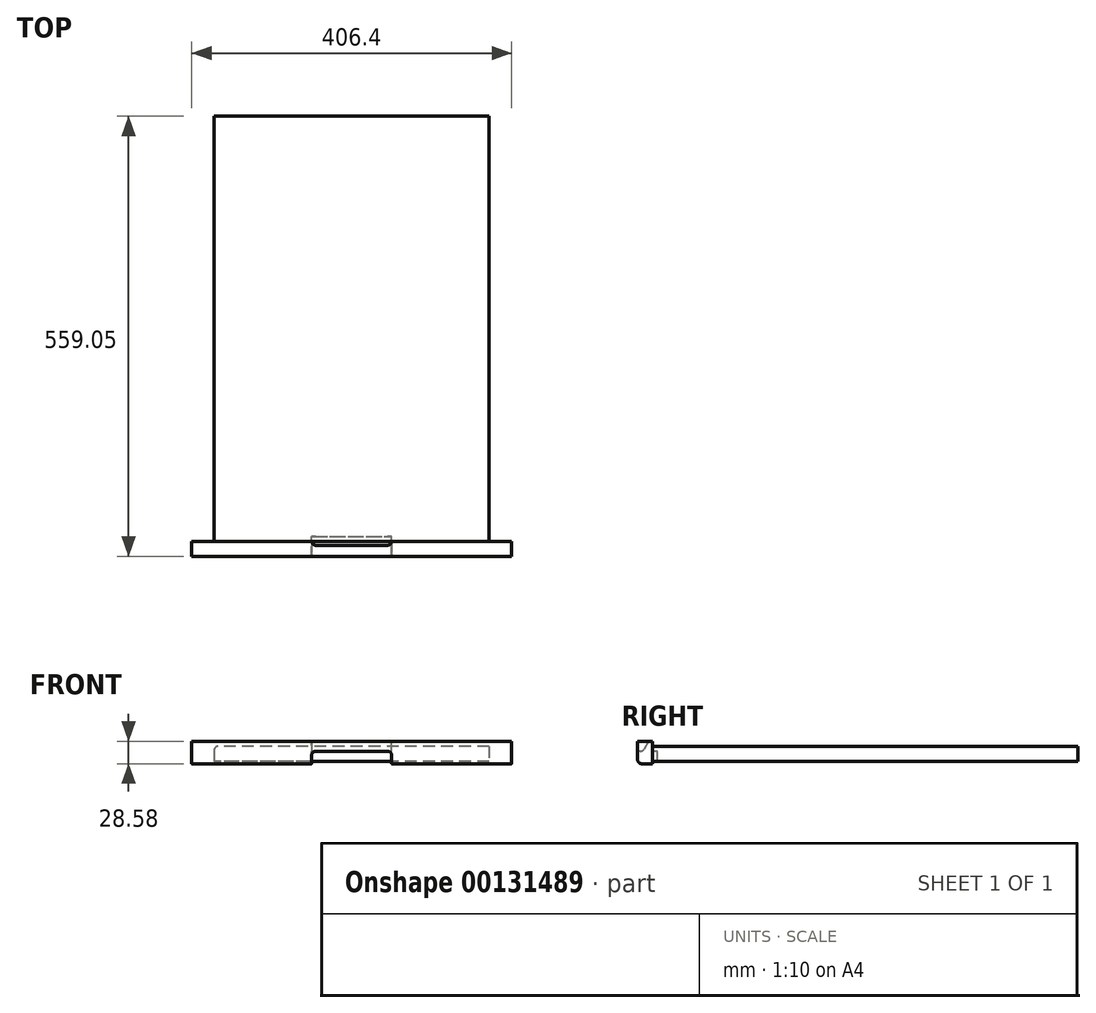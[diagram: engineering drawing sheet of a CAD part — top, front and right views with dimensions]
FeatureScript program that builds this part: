
annotation { "Feature Type Name" : "Feature", "Feature Type Description" : "" }
export const myFeature = defineFeature(function(context is Context, id is Id, definition is map)
    precondition{}
    {
        {
            var Q0;
            Q0=qCreatedBy(makeId("Top.planeOp"),FACE);
            var sketch = newSketch(context, id + "F0", { "sketchPlane" : qUnion([Q0])});
            skLineSegment(sketch, "E0.bottom", {"start": v(174.63, 270) * mm, "end": v(-174.62, 270) * mm});
            skLineSegment(sketch, "E0.top", {"start": v(174.63, -270) * mm, "end": v(-174.63, -270) * mm});
            skLineSegment(sketch, "E0.left", {"start": v(174.63, 270) * mm, "end": v(174.63, -270) * mm});
            skLineSegment(sketch, "E0.right", {"start": v(-174.62, 270) * mm, "end": v(-174.63, -270) * mm});
            skPoint(sketch, "E0.middle", {"position": v(0, 0) * mm});
            skSolve(sketch);
        }
        {
            var Q0;
            Q0 = qSketchRegion(id + "F0", true);
            extrude(context, id + "F1", {"entities" : qUnion([Q0]), "depth" : 19.05 * mm});
        }
        {
            var Q0;
            Q0=makeQuery(id+"F1.opExtrude","SWEPT_FACE",FACE,{"disambiguationData":[OSD([sQuery(id+"F0.wireOp",EDGE,"E0.top")])]});
            var sketch = newSketch(context, id + "F2", { "sketchPlane" : qUnion([Q0])});
            skLineSegment(sketch, "E1.bottom", {"start": v(-203.2, 25.4) * mm, "end": v(203.2, 25.4) * mm});
            skLineSegment(sketch, "E1.top", {"start": v(-203.2, -3.18) * mm, "end": v(203.2, -3.18) * mm});
            skLineSegment(sketch, "E1.left", {"start": v(-203.2, 25.4) * mm, "end": v(-203.2, -3.17) * mm});
            skLineSegment(sketch, "E1.right", {"start": v(203.2, 25.4) * mm, "end": v(203.2, -3.17) * mm});
            skLineSegment(sketch, "E2", {"start": v(-203.2, 11.11) * mm, "end": v(-174.63, 11.11) * mm, "construction": true});
            skLineSegment(sketch, "E3.0", {"start": v(-174.63, 19.05) * mm, "end": v(-174.63, 0) * mm, "construction": true});
            skLineSegment(sketch, "E4.0", {"start": v(174.63, 19.05) * mm, "end": v(-174.63, 19.05) * mm, "construction": true});
            skLineSegment(sketch, "E5.0", {"start": v(174.63, 19.05) * mm, "end": v(174.63, 0) * mm, "construction": true});
            skLineSegment(sketch, "E6.0", {"start": v(174.63, 0) * mm, "end": v(-174.63, 0) * mm, "construction": true});
            skLineSegment(sketch, "E7.trimOffspring", {"start": v(174.63, 11.11) * mm, "end": v(203.2, 11.11) * mm, "construction": true});
            skSolve(sketch);
        }
        {
            var Q0;
            Q0 = qSketchRegion(id + "F2", true);
            extrude(context, id + "F3", {"entities" : qUnion([Q0]), "depth" : 19.05 * mm});
        }
        {
            var Q0;
            Q0=makeQuery(id+"F3.opExtrude","CAP_FACE",FACE,{"disambiguationData":[OSD([sQuery(id+"F2.wireOp",EDGE,"E1.bottom"),sQuery(id+"F2.wireOp",EDGE,"E1.top"),sQuery(id+"F2.wireOp",EDGE,"E1.left"),sQuery(id+"F2.wireOp",EDGE,"E1.right")])],"isStart":false});
            var sketch = newSketch(context, id + "F4", { "sketchPlane" : qUnion([Q0])});
            skLineSegment(sketch, "E8.bottom", {"start": v(-50.8, -3.18) * mm, "end": v(50.8, -3.18) * mm});
            skLineSegment(sketch, "E8.top", {"start": v(-50.8, 12.7) * mm, "end": v(50.8, 12.7) * mm});
            skLineSegment(sketch, "E8.left", {"start": v(-50.8, -3.18) * mm, "end": v(-50.8, 12.7) * mm});
            skLineSegment(sketch, "E8.right", {"start": v(50.8, -3.18) * mm, "end": v(50.8, 12.7) * mm});
            skLineSegment(sketch, "E9", {"start": v(50.8, 12.7) * mm, "end": v(203.2, 12.7) * mm, "construction": true});
            skLineSegment(sketch, "E10", {"start": v(-50.8, 12.7) * mm, "end": v(-203.2, 12.7) * mm, "construction": true});
            skSolve(sketch);
        }
        {
            var Q0;
            Q0 = qSketchRegion(id + "F4", true);
            extrude(context, id + "F5", {"entities" : qUnion([Q0]), "operationType" : NewBodyOperationType.REMOVE, "oppositeDirection" : true, "depth" : 25.4 * mm});
        }
        {
            var Q0;
            Q0=makeQuery(id+"F5.boolean.opBoolean","INTERSECT",EDGE,{"derivedFrom":[makeQuery(id+"F3.opExtrude","CAP_FACE",FACE,{"disambiguationData":[OSD([sQuery(id+"F2.wireOp",EDGE,"E1.bottom"),sQuery(id+"F2.wireOp",EDGE,"E1.top"),sQuery(id+"F2.wireOp",EDGE,"E1.left"),sQuery(id+"F2.wireOp",EDGE,"E1.right")])],"isStart":true}),makeQuery(id+"F5.opExtrude","SWEPT_FACE",FACE,{"disambiguationData":[OSD([sQuery(id+"F4.wireOp",EDGE,"E8.top")])]})]});
            chamfer(context, id + "F6", {"entities" : qUnion([Q0]), "chamferType" : ChamferType.OFFSET_ANGLE, "width" : 21.59 * mm, "oppositeDirection" : false, "angle" : 30 * degree, "tangentPropagation" : true});
        }
        {
            var Q0;
            Q0=makeQuery(id+"F5.boolean.opBoolean","COPY",EDGE,{"derivedFrom":makeQuery(id+"F5.opExtrude","SWEPT_EDGE",EDGE,{"disambiguationData":[OSD([sQuery(id+"F2.wireOp",EDGE,"E1.top"),sQuery(id+"F4.wireOp",EDGE,"E8.bottom"),sQuery(id+"F4.wireOp",EDGE,"E8.left")])]})});
            var Q1;
            Q1=makeQuery(id+"F5.boolean.opBoolean","COPY",EDGE,{"derivedFrom":makeQuery(id+"F5.opExtrude","SWEPT_EDGE",EDGE,{"disambiguationData":[OSD([sQuery(id+"F2.wireOp",EDGE,"E1.top"),sQuery(id+"F4.wireOp",EDGE,"E8.bottom"),sQuery(id+"F4.wireOp",EDGE,"E8.right")])]})});
            var Q2;
            Q2=makeQuery(id+"F6.opChamfer","BLEND_EDGE",EDGE,{"blendedFrom":[makeQuery(id+"F5.boolean.opBoolean","INTERSECT",EDGE,{"derivedFrom":[makeQuery(id+"F3.opExtrude","CAP_FACE",FACE,{"disambiguationData":[OSD([sQuery(id+"F2.wireOp",EDGE,"E1.bottom"),sQuery(id+"F2.wireOp",EDGE,"E1.top"),sQuery(id+"F2.wireOp",EDGE,"E1.left"),sQuery(id+"F2.wireOp",EDGE,"E1.right")])],"isStart":true}),makeQuery(id+"F5.opExtrude","SWEPT_FACE",FACE,{"disambiguationData":[OSD([sQuery(id+"F4.wireOp",EDGE,"E8.top")])]})]}),makeQuery(id+"F5.boolean.opBoolean","COPY",FACE,{"derivedFrom":makeQuery(id+"F5.opExtrude","SWEPT_FACE",FACE,{"disambiguationData":[OSD([sQuery(id+"F4.wireOp",EDGE,"E8.right")])]})})],"blendedInto":[makeQuery(id+"F5.boolean.opBoolean","COPY",FACE,{"derivedFrom":makeQuery(id+"F5.opExtrude","SWEPT_FACE",FACE,{"disambiguationData":[OSD([sQuery(id+"F4.wireOp",EDGE,"E8.right")])]})})]});
            var Q3;
            Q3=makeQuery(id+"FXZCt5cPQfUOwaD_1.boolean.opBoolean","COPY",EDGE,{"derivedFrom":makeQuery(id+"FXZCt5cPQfUOwaD_1.opExtrude","SWEPT_EDGE",EDGE,{"disambiguationData":[OSD([sQuery(id+"FGhspWLTeAS0HlX_1.wireOp",EDGE,"FRW7Mbth-WyWN-BmpX-e6wB-hWx09g5650vy.bottom"),sQuery(id+"FGhspWLTeAS0HlX_1.wireOp",EDGE,"FRW7Mbth-WyWN-BmpX-e6wB-hWx09g5650vy.right")])]})});
            var Q4;
            Q4=makeQuery(id+"F1.opExtrude","CAP_EDGE",EDGE,{"disambiguationData":[OSD([sQuery(id+"F0.wireOp",EDGE,"E0.right")])],"isStart":false});
            var Q5;
            Q5=makeQuery(id+"FXZCt5cPQfUOwaD_1.boolean.opBoolean","COPY",EDGE,{"derivedFrom":makeQuery(id+"FXZCt5cPQfUOwaD_1.opExtrude","CAP_EDGE",EDGE,{"disambiguationData":[OSD([sQuery(id+"FGhspWLTeAS0HlX_1.wireOp",EDGE,"FRW7Mbth-WyWN-BmpX-e6wB-hWx09g5650vy.right")])],"isStart":true})});
            var Q6;
            Q6=makeQuery(id+"F6.opChamfer","BLEND_EDGE",EDGE,{"blendedFrom":[makeQuery(id+"F5.boolean.opBoolean","INTERSECT",EDGE,{"derivedFrom":[makeQuery(id+"F3.opExtrude","CAP_FACE",FACE,{"disambiguationData":[OSD([sQuery(id+"F2.wireOp",EDGE,"E1.bottom"),sQuery(id+"F2.wireOp",EDGE,"E1.top"),sQuery(id+"F2.wireOp",EDGE,"E1.left"),sQuery(id+"F2.wireOp",EDGE,"E1.right")])],"isStart":true}),makeQuery(id+"F5.opExtrude","SWEPT_FACE",FACE,{"disambiguationData":[OSD([sQuery(id+"F4.wireOp",EDGE,"E8.top")])]})]}),makeQuery(id+"F5.boolean.opBoolean","COPY",FACE,{"derivedFrom":makeQuery(id+"F5.opExtrude","SWEPT_FACE",FACE,{"disambiguationData":[OSD([sQuery(id+"F4.wireOp",EDGE,"E8.left")])]})})],"blendedInto":[makeQuery(id+"F5.boolean.opBoolean","COPY",FACE,{"derivedFrom":makeQuery(id+"F5.opExtrude","SWEPT_FACE",FACE,{"disambiguationData":[OSD([sQuery(id+"F4.wireOp",EDGE,"E8.left")])]})})]});
            var Q7;
            Q7=makeQuery(id+"F5.boolean.opBoolean","COPY",EDGE,{"derivedFrom":makeQuery(id+"F5.opExtrude","SWEPT_EDGE",EDGE,{"disambiguationData":[OSD([sQuery(id+"F4.wireOp",EDGE,"E8.top"),sQuery(id+"F4.wireOp",EDGE,"E8.left")])]})});
            var Q8;
            {var subQ0=makeQuery(id+"F5.opExtrude","SWEPT_FACE",FACE,{"disambiguationData":[OSD([sQuery(id+"F4.wireOp",EDGE,"E8.top")])]});Q8=makeQuery(id+"F6.opChamfer","BLEND_EDGE",EDGE,{"blendedFrom":[makeQuery(id+"F5.boolean.opBoolean","INTERSECT",EDGE,{"derivedFrom":[makeQuery(id+"F3.opExtrude","CAP_FACE",FACE,{"disambiguationData":[OSD([sQuery(id+"F2.wireOp",EDGE,"E1.bottom"),sQuery(id+"F2.wireOp",EDGE,"E1.top"),sQuery(id+"F2.wireOp",EDGE,"E1.left"),sQuery(id+"F2.wireOp",EDGE,"E1.right")])],"isStart":true}),subQ0]}),makeQuery(id+"F5.boolean.opBoolean","COPY",FACE,{"derivedFrom":subQ0})],"blendedInto":[makeQuery(id+"F5.boolean.opBoolean","COPY",FACE,{"derivedFrom":subQ0})]});}
            var Q9;
            Q9=makeQuery(id+"F5.boolean.opBoolean","COPY",EDGE,{"derivedFrom":makeQuery(id+"F5.opExtrude","CAP_EDGE",EDGE,{"disambiguationData":[OSD([sQuery(id+"F4.wireOp",EDGE,"E8.top")])],"isStart":true})});
            var Q10;
            Q10=makeQuery(id+"F5.boolean.opBoolean","COPY",EDGE,{"derivedFrom":makeQuery(id+"F5.opExtrude","SWEPT_EDGE",EDGE,{"disambiguationData":[OSD([sQuery(id+"F4.wireOp",EDGE,"E8.top"),sQuery(id+"F4.wireOp",EDGE,"E8.right")])]})});
            var Q11;
            {var subQ0=sQuery(id+"F2.wireOp",EDGE,"E1.right");var subQ1=sQuery(id+"F2.wireOp",EDGE,"E1.left");var subQ2=sQuery(id+"F2.wireOp",EDGE,"E1.top");var subQ3=sQuery(id+"F2.wireOp",EDGE,"E1.bottom");Q11=makeQuery(id+"F6.opChamfer","BLEND_EDGE",EDGE,{"blendedFrom":[makeQuery(id+"F5.boolean.opBoolean","INTERSECT",EDGE,{"derivedFrom":[makeQuery(id+"F3.opExtrude","CAP_FACE",FACE,{"disambiguationData":[OSD([subQ3,subQ2,subQ1,subQ0])],"isStart":true}),makeQuery(id+"F5.opExtrude","SWEPT_FACE",FACE,{"disambiguationData":[OSD([sQuery(id+"F4.wireOp",EDGE,"E8.top")])]})]}),makeQuery(id+"F3.opExtrude","CAP_FACE",FACE,{"disambiguationData":[OSD([subQ3,subQ2,subQ1,subQ0])],"isStart":false})],"blendedInto":[makeQuery(id+"F3.opExtrude","CAP_FACE",FACE,{"disambiguationData":[OSD([subQ3,subQ2,subQ1,subQ0])],"isStart":false})]});}
            var Q12;
            {var subQ0=sQuery(id+"F2.wireOp",EDGE,"E1.right");var subQ1=sQuery(id+"F2.wireOp",EDGE,"E1.top");Q12=makeQuery(id+"F5.boolean.opBoolean","SPLIT",EDGE,{"disambiguationData":[TD([makeQuery(id+"F3.opExtrude","SWEPT_FACE",FACE,{"disambiguationData":[OSD([subQ0])]})])],"derivedFrom":makeQuery(id+"F3.opExtrude","CAP_EDGE",EDGE,{"disambiguationData":[OSD([subQ1])],"isStart":false})});}
            var Q13;
            {var subQ0=sQuery(id+"F2.wireOp",EDGE,"E1.left");var subQ1=sQuery(id+"F2.wireOp",EDGE,"E1.top");Q13=makeQuery(id+"F5.boolean.opBoolean","SPLIT",EDGE,{"disambiguationData":[TD([makeQuery(id+"F3.opExtrude","SWEPT_FACE",FACE,{"disambiguationData":[OSD([subQ0])]})])],"derivedFrom":makeQuery(id+"F3.opExtrude","CAP_EDGE",EDGE,{"disambiguationData":[OSD([subQ1])],"isStart":false})});}
            fillet(context, id + "F7", {"entities" : qUnion([Q0, Q1, Q2, Q3, Q4, Q5, Q6, Q7, Q8, Q9, Q10, Q11, Q12, Q13]), "radius" : 5.08 * mm, "tangentPropagation" : true, "allowEdgeOverflow" : false});
        }
    });
